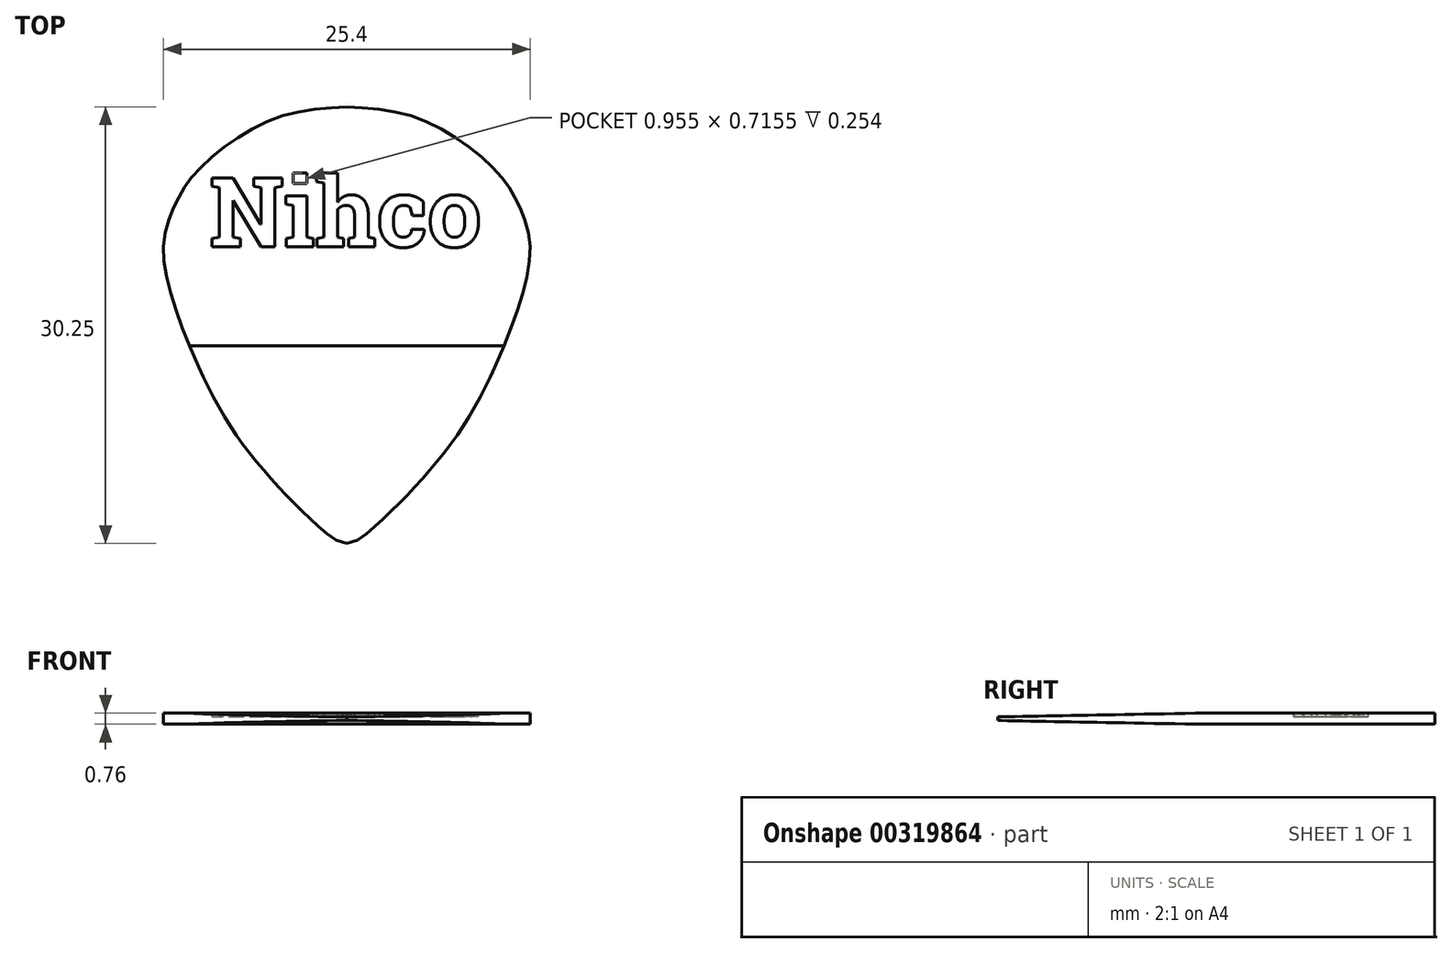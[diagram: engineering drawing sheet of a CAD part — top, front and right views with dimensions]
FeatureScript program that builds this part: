
annotation { "Feature Type Name" : "Feature", "Feature Type Description" : "" }
export const myFeature = defineFeature(function(context is Context, id is Id, definition is map)
    precondition{}
    {
        {
            var Q0;
            Q0=qCreatedBy(makeId("Top.planeOp"),FACE);
            var sketch = newSketch(context, id + "F0", { "sketchPlane" : qUnion([Q0])});
            skLineSegment(sketch, "E0", {"start": v(0, 20.02) * mm, "end": v(0, -20.48) * mm, "construction": true});
            skFitSpline(sketch, "E1", {"points": [v(0, 16.57) * mm, v(4.08, 16.05) * mm, v(7.9, 14.19) * mm, v(10.67, 11.76) * mm, v(11.83, 9.91) * mm, v(12.66, 7.42) * mm, v(12.2, 3.69) * mm, v(10.2, -1.55) * mm, v(7.72, -6.06) * mm, v(5.4, -8.99) * mm, v(3.67, -10.86) * mm, v(1.36, -13) * mm, v(0.56, -13.55) * mm, v(0.3, -13.62) * mm, v(0, -13.68) * mm], "startDerivative": vector(44.54, -3.36) * mm, "endDerivative": vector(-12.7, -2.35) * mm});
            skFitSpline(sketch, "E2.MirrorCS", {"points": [v(0, 16.57) * mm, v(-4.08, 16.05) * mm, v(-7.9, 14.19) * mm, v(-10.67, 11.76) * mm, v(-11.83, 9.91) * mm, v(-12.66, 7.42) * mm, v(-12.2, 3.69) * mm, v(-10.2, -1.55) * mm, v(-7.72, -6.06) * mm, v(-5.4, -8.99) * mm, v(-3.67, -10.86) * mm, v(-1.36, -13) * mm, v(-0.56, -13.55) * mm, v(-0.3, -13.62) * mm, v(0, -13.68) * mm], "startDerivative": vector(-44.54, -3.36) * mm, "endDerivative": vector(12.7, -2.35) * mm});
            skSolve(sketch);
        }
        {
            var Q0;
            Q0 = qSketchRegion(id + "F0", true);
            extrude(context, id + "F1", {"entities" : qUnion([Q0]), "depth" : 0.76 * mm});
        }
        {
            var Q0;
            Q0=makeQuery(id+"F1.opExtrude","CAP_FACE",FACE,{"disambiguationData":[OSD([sQuery(id+"F0.wireOp",EDGE,"E1"),sQuery(id+"F0.wireOp",EDGE,"E2.MirrorCS")])],"isStart":false});
            var sketch = newSketch(context, id + "F2", { "sketchPlane" : qUnion([Q0])});
            skText(sketch, "E3", { "text": "Nihco\n", "fontName": "RobotoSlab-Bold.ttf"});
            const initialGuessF2  = {"E3": [-0.00953, 0.00687, 1, 0, 0.00482]};
            skSetInitialGuess(sketch, initialGuessF2);
            skSolve(sketch);
        }
        {
            var Q0;
            Q0 = qSketchRegion(id + "F2", true);
            extrude(context, id + "F3", {"entities" : qUnion([Q0]), "operationType" : NewBodyOperationType.REMOVE, "oppositeDirection" : true, "depth" : 0.25 * mm});
        }
        {
            var Q0;
            Q0=qCreatedBy(makeId("Right.planeOp"),FACE);
            var sketch = newSketch(context, id + "F4", { "sketchPlane" : qUnion([Q0])});
            skFitSpline(sketch, "E4.0.0", {"points": [v(-13.68, 0) * mm, v(-13.66, 0) * mm, v(-13.62, 0) * mm, v(-13.56, 0) * mm, v(-12.97, 0) * mm, v(-10.8, 0) * mm, v(-9, 0) * mm, v(-6.03, 0) * mm, v(-1.6, 0) * mm, v(3.53, 0) * mm, v(7.36, 0) * mm, v(9.95, 0) * mm, v(11.9, 0) * mm, v(14.37, 0) * mm, v(16.34, 0) * mm, v(16.47, 0) * mm, v(16.57, 0) * mm]});
            skFitSpline(sketch, "E4.0.2", {"points": [v(16.57, 0.76) * mm, v(16.47, 0.76) * mm, v(16.34, 0.76) * mm, v(14.37, 0.76) * mm, v(11.9, 0.76) * mm, v(9.95, 0.76) * mm, v(7.36, 0.76) * mm, v(3.53, 0.76) * mm, v(-1.6, 0.76) * mm, v(-6.03, 0.76) * mm, v(-9, 0.76) * mm, v(-10.8, 0.76) * mm, v(-12.97, 0.76) * mm, v(-13.56, 0.76) * mm, v(-13.62, 0.76) * mm, v(-13.66, 0.76) * mm, v(-13.68, 0.76) * mm]});
            skLineSegment(sketch, "E4.0.3", {"start": v(-13.68, 0.76) * mm, "end": v(-13.68, 0) * mm});
            skLineSegment(sketch, "E5", {"start": v(-13.68, 0.38) * mm, "end": v(16.57, 0.38) * mm, "construction": true});
            skLineSegment(sketch, "E6", {"start": v(-13.68, 0.5) * mm, "end": v(0, 0.76) * mm});
            skLineSegment(sketch, "E7.MirrorCS", {"start": v(-13.68, 0.25) * mm, "end": v(0, 0) * mm});
            skPoint(sketch, "E8.orphan", {"position": v(16.57, 0) * mm});
            skPoint(sketch, "E4.0.1.end.orphan", {"position": v(16.57, 0.76) * mm});
            skSolve(sketch);
        }
        {
            var Q0;
            Q0 = qSketchRegion(id + "F4", true);
            extrude(context, id + "F5", {"entities" : qUnion([Q0]), "operationType" : NewBodyOperationType.REMOVE, "oppositeDirection" : true, "depth" : 25.4 * mm, "hasSecondDirection" : true, "secondDirectionOppositeDirection" : false, "secondDirectionDepth" : 25.4 * mm});
        }
    });
